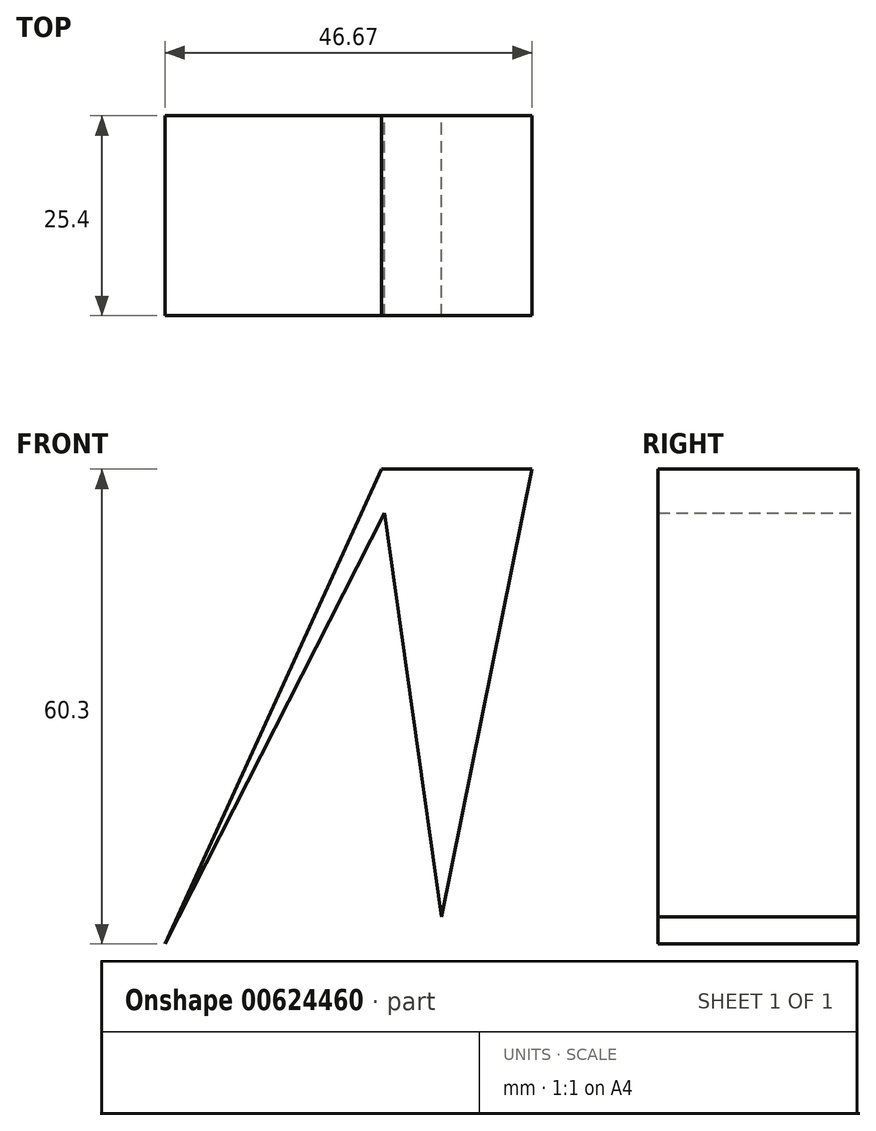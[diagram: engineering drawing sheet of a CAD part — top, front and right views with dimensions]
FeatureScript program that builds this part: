
annotation { "Feature Type Name" : "Feature", "Feature Type Description" : "" }
export const myFeature = defineFeature(function(context is Context, id is Id, definition is map)
    precondition{}
    {
        {
            var Q0;
            Q0=qCreatedBy(makeId("Front.planeOp"),FACE);
            var sketch = newSketch(context, id + "F0", { "sketchPlane" : qUnion([Q0])});
            skLineSegment(sketch, "E0", {"start": v(-27.5, -30.55) * mm, "end": v(0, 29.75) * mm});
            skLineSegment(sketch, "E1", {"start": v(0.42, 24.2) * mm, "end": v(-27.5, -30.55) * mm});
            skLineSegment(sketch, "E2", {"start": v(0.42, 24.2) * mm, "end": v(7.64, -27.1) * mm});
            skLineSegment(sketch, "E3", {"start": v(7.64, -27.1) * mm, "end": v(19.16, 29.75) * mm});
            skLineSegment(sketch, "E4", {"start": v(0, 29.75) * mm, "end": v(19.16, 29.75) * mm});
            skSolve(sketch);
        }
        {
            var Q0;
            Q0 = qSketchRegion(id + "F0", true);
            extrude(context, id + "F1", {"entities" : qUnion([Q0]), "depth" : 25.4 * mm, "offsetDistance" : 25.4 * mm});
        }
    });
